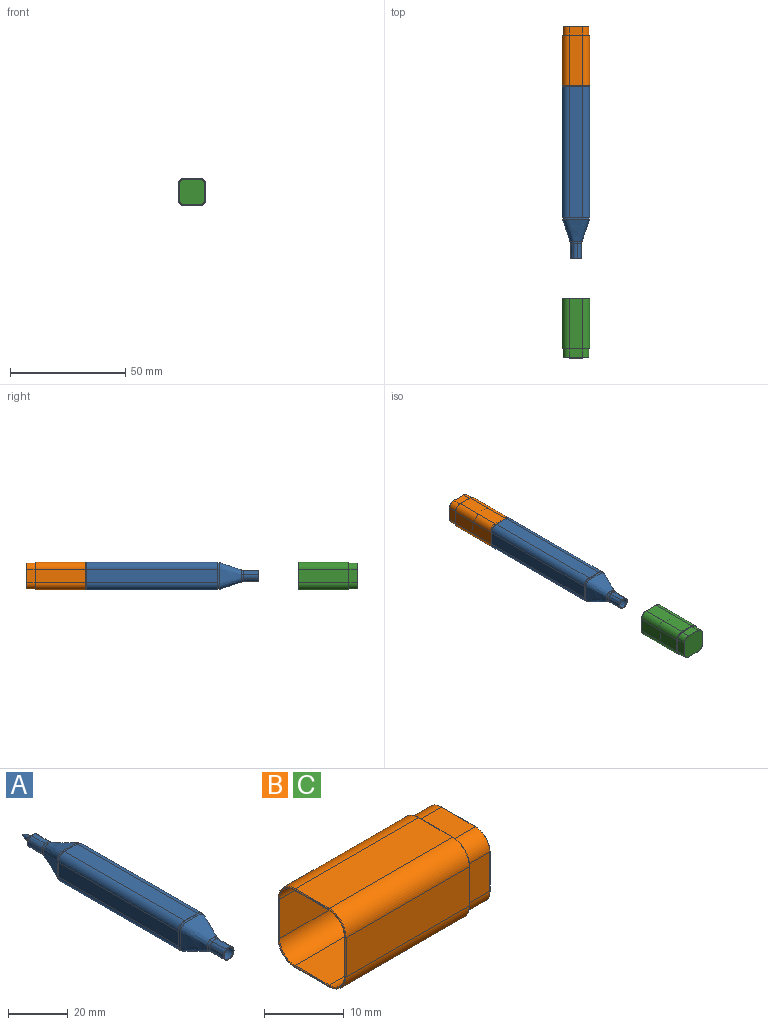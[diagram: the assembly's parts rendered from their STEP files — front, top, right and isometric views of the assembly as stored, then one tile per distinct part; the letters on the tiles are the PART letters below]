
ASSEMBLY  parts=3 mates=1
PART A: 104 faces, bbox 12x98.1x12 mm
  f0: plane 57x6mm, normal (0,0,-1), area 342mm2, adj f1,f3,f7,f9
  f1: plane 12x12mm, normal (0,1,0), area 8mm2, adj f0,f2,f4,f5,f6,f7,f8,f9
  f2: plane 57x6mm, normal (0,0,1), area 342mm2, adj f1,f3,f6,f8
  f3: plane 12x12mm, normal (0,-1,0), area 8mm2, adj f0,f2,f4,f5,f6,f7,f8,f9
  f4: plane 57x6mm, normal (1,0,0), area 342mm2, adj f1,f3,f8,f9
  f5: plane 57x6mm, normal (-1,0,0), area 342mm2, adj f1,f3,f6,f7
  f6: cylinder r=3mm len=57mm, axis (0,-1,0), area 268.6mm2, adj f1,f2,f3,f5
  f7: cylinder r=3mm len=57mm, axis (0,1,0), area 268.6mm2, adj f0,f1,f3,f5
  f8: cylinder r=3mm len=57mm, axis (0,1,0), area 268.6mm2, adj f1,f2,f3,f4
  f9: cylinder r=3mm len=57mm, axis (0,-1,0), area 268.6mm2, adj f0,f1,f3,f4
  f10: plane 6x0.06mm, normal (0,0,-1), area 0.4mm2, adj f1,f11,f17,f18
  f11: cylinder r=2.81mm len=2.81mm, axis (0,-1,0), area 0.3mm2, adj f1,f10,f12,f18
  f12: plane 6x0.06mm, normal (-1,0,0), area 0.4mm2, adj f1,f11,f13,f18
  f13: cylinder r=2.81mm len=2.81mm, axis (0,-1,0), area 0.3mm2, adj f1,f12,f14,f18
  f14: plane 6x0.06mm, normal (0,0,1), area 0.4mm2, adj f1,f13,f15,f18
  f15: cylinder r=2.81mm len=2.81mm, axis (0,-1,0), area 0.3mm2, adj f1,f14,f16,f18
  f16: plane 6x0.06mm, normal (1,0,0), area 0.4mm2, adj f1,f15,f17,f18
  f17: cylinder r=2.81mm len=2.81mm, axis (0,-1,0), area 0.3mm2, adj f1,f10,f16,f18
  f18: plane 11.62x11.62mm, normal (0,1,0), area 4.1mm2, adj f10,f11,f12,f13,f14,f15,f16,f17
  f19: plane 6x0.8mm, normal (1,0,0), area 4.8mm2, adj f18,f20,f26,f45
  f20: cylinder r=2.71mm len=2.71mm, axis (0,-1,0), area 3.4mm2, adj f18,f19,f21,f45
  f21: plane 6x0.8mm, normal (0,0,-1), area 4.8mm2, adj f18,f20,f22,f45
  f22: cylinder r=2.71mm len=2.71mm, axis (0,-1,0), area 3.4mm2, adj f18,f21,f23,f45
  f23: plane 6x0.8mm, normal (-1,0,0), area 4.8mm2, adj f18,f22,f24,f45
  f24: cylinder r=2.71mm len=2.71mm, axis (0,-1,0), area 3.4mm2, adj f18,f23,f25,f45
  f25: plane 6x0.8mm, normal (0,0,1), area 4.8mm2, adj f18,f24,f26,f45
  f26: cylinder r=2.71mm len=2.71mm, axis (0,-1,0), area 3.4mm2, adj f18,f19,f25,f45
  f27: plane 6x0.86mm, normal (1,0,0), area 5.2mm2, adj f3,f28,f34,f35
  f28: cylinder r=2.81mm len=2.81mm, axis (0,1,0), area 3.8mm2, adj f3,f27,f29,f35
  f29: plane 6x0.86mm, normal (0,0,1), area 5.2mm2, adj f3,f28,f30,f35
  f30: cylinder r=2.81mm len=2.81mm, axis (0,1,0), area 3.8mm2, adj f3,f29,f31,f35
  f31: plane 6x0.86mm, normal (-1,0,0), area 5.2mm2, adj f3,f30,f32,f35
  f32: cylinder r=2.81mm len=2.81mm, axis (0,1,0), area 3.8mm2, adj f3,f31,f33,f35
  f33: plane 6x0.86mm, normal (0,0,-1), area 5.2mm2, adj f3,f32,f34,f35
  f34: cylinder r=2.81mm len=2.81mm, axis (0,1,0), area 3.8mm2, adj f3,f27,f33,f35
  f35: bspline ~11.62x11.62mm, area 296.6mm2, adj f27,f28,f29,f30,f31,f32,f33,f34
  f36: extruded ~6.53x1.46mm, area 12.8mm2, adj f37,f43,f44,f91
  f37: extruded ~6.53x1.91mm, area 12.8mm2, adj f36,f38,f44,f93
  f38: extruded ~6.53x1.46mm, area 12.8mm2, adj f37,f39,f44,f92
  f39: extruded ~6.53x1.91mm, area 12.8mm2, adj f38,f40,f44,f90
  f40: extruded ~6.53x1.46mm, area 12.8mm2, adj f39,f41,f44,f88
  f41: extruded ~6.53x1.91mm, area 12.8mm2, adj f40,f42,f44,f86
  f42: extruded ~6.53x1.46mm, area 12.8mm2, adj f41,f43,f44,f87
  f43: extruded ~6.53x1.91mm, area 12.8mm2, adj f36,f42,f44,f89
  f44: plane 5.04x5.04mm, normal (0,-1,0), area 4.4mm2, adj f36,f37,f38,f39,f40,f41,f42,f43
  f45: bspline ~11.42x11.42mm, area 292.4mm2, adj f19,f20,f21,f22,f23,f24,f25,f26
  f46: extruded ~6.52x1.47mm, area 12.8mm2, adj f47,f53,f72,f96
  f47: extruded ~6.52x1.91mm, area 12.8mm2, adj f46,f48,f73,f94
  f48: extruded ~6.52x1.47mm, area 12.8mm2, adj f47,f49,f75,f95
  f49: extruded ~6.52x1.91mm, area 12.8mm2, adj f48,f50,f77,f97
  f50: extruded ~6.52x1.47mm, area 12.8mm2, adj f49,f51,f79,f99
  f51: extruded ~6.52x1.91mm, area 12.8mm2, adj f50,f52,f78,f101
  f52: extruded ~6.52x1.47mm, area 12.8mm2, adj f51,f53,f76,f100
  f53: extruded ~6.52x1.91mm, area 12.8mm2, adj f46,f52,f74,f98
  f54: bspline ~4.94x4.94mm, area 20mm2, adj f64,f65,f66,f67,f68,f69,f70,f71
  f55: extruded ~0.76x0.64mm, area 0.1mm2, adj f56,f62,f63,f70
  f56: extruded ~0.99x0.15mm, area 0.1mm2, adj f55,f57,f63,f68
  f57: extruded ~0.76x0.64mm, area 0.1mm2, adj f56,f58,f63,f66
  f58: extruded ~0.99x0.15mm, area 0.1mm2, adj f57,f59,f63,f64
  f59: extruded ~0.76x0.64mm, area 0.1mm2, adj f58,f60,f63,f65
  f60: extruded ~0.99x0.15mm, area 0.1mm2, adj f59,f61,f63,f67
  f61: extruded ~0.76x0.64mm, area 0.1mm2, adj f60,f62,f63,f69
  f62: extruded ~0.99x0.15mm, area 0.1mm2, adj f55,f61,f63,f71
  f63: plane 2.6x2.6mm, normal (0,1,0), area 1.9mm2, adj f55,f56,f57,f58,f59,f60,f61,f62
  f64: bspline ~1.13x0.17mm, area 0mm2, adj f54,f58,f65,f66
  f65: bspline ~0.85x0.75mm, area 0mm2, adj f54,f59,f64,f67
  f66: bspline ~0.85x0.75mm, area 0mm2, adj f54,f57,f64,f68
  f67: bspline ~1.13x0.17mm, area 0mm2, adj f54,f60,f65,f69
  f68: bspline ~1.13x0.17mm, area 0mm2, adj f54,f56,f66,f70
  f69: bspline ~0.85x0.75mm, area 0mm2, adj f54,f61,f67,f71
  f70: bspline ~0.85x0.75mm, area 0mm2, adj f54,f55,f68,f71
  f71: bspline ~1.13x0.17mm, area 0mm2, adj f54,f62,f69,f70
  f72: bspline ~1.91x1.6mm, area 0.1mm2, adj f46,f54,f73,f74
  f73: bspline ~2.47x0.46mm, area 0.1mm2, adj f47,f54,f72,f75
  f74: bspline ~2.47x0.46mm, area 0.1mm2, adj f53,f54,f72,f76
  f75: bspline ~1.91x1.6mm, area 0.1mm2, adj f48,f54,f73,f77
  f76: bspline ~1.91x1.6mm, area 0.1mm2, adj f52,f54,f74,f78
  f77: bspline ~2.47x0.46mm, area 0.1mm2, adj f49,f54,f75,f79
  f78: bspline ~2.47x0.46mm, area 0.1mm2, adj f51,f54,f76,f79
  f79: bspline ~1.91x1.6mm, area 0.1mm2, adj f50,f54,f77,f78
  f80: cylinder r=1.04mm len=25mm, axis (0,1,0), area 164.1mm2, adj f63,f81
  f81: plane 2.09x2.09mm, normal (0,1,0), area 0.3mm2, adj f80,f82
  f82: cylinder r=1mm len=25.5mm, axis (0,-1,0), area 160.2mm2, adj f81,f84
  f83: plane 0.03x0.03mm, normal (0,1,0), area 0mm2, adj f85
  f84: bspline ~3.37x2mm, area 14.2mm2, adj f82,f85
  f85: bspline ~0.13x0.13mm, area 0mm2, adj f83,f84
  f86: bspline ~2.32x1.15mm, area 2.1mm2, adj f35,f41,f87,f88
  f87: bspline ~1.66x1.49mm, area 2.4mm2, adj f35,f42,f86,f89
  f88: bspline ~1.66x1.49mm, area 2.4mm2, adj f35,f40,f86,f90
  f89: bspline ~2.32x1.15mm, area 2.1mm2, adj f35,f43,f87,f91
  f90: bspline ~2.32x1.15mm, area 2.1mm2, adj f35,f39,f88,f92
  f91: bspline ~1.66x1.49mm, area 2.4mm2, adj f35,f36,f89,f93
  f92: bspline ~1.66x1.49mm, area 2.4mm2, adj f35,f38,f90,f93
  f93: bspline ~2.38x1.16mm, area 2.1mm2, adj f35,f37,f91,f92
  f94: bspline ~2.31x1.13mm, area 2.1mm2, adj f45,f47,f95,f96
  f95: bspline ~1.66x1.47mm, area 2.4mm2, adj f45,f48,f94,f97
  f96: bspline ~1.66x1.47mm, area 2.4mm2, adj f45,f46,f94,f98
  f97: bspline ~2.31x1.13mm, area 2.1mm2, adj f45,f49,f95,f99
  f98: bspline ~2.31x1.13mm, area 2.1mm2, adj f45,f53,f96,f100
  f99: bspline ~1.66x1.47mm, area 2.4mm2, adj f45,f50,f97,f101
  f100: bspline ~1.66x1.47mm, area 2.4mm2, adj f45,f52,f98,f101
  f101: bspline ~2.31x1.13mm, area 2.1mm2, adj f45,f51,f99,f100
  f102: cylinder r=2.2mm len=25mm, axis (0,-1,0), area 346.2mm2, adj f44,f103
  f103: plane 4.41x4.41mm, normal (0,-1,0), area 15.3mm2, adj f102
PART B: 73 faces, bbox 26x14x14 mm
  f0: plane 21.8x6mm, normal (0,1,0), area 130.8mm2, adj f1,f7,f43,f51
  f1: cylinder r=3mm len=21.8mm, axis (-1,0,0), area 102.7mm2, adj f0,f2,f41,f49
  f2: plane 21.8x6mm, normal (0,0,1), area 130.8mm2, adj f1,f3,f40,f48
  f3: cylinder r=3mm len=21.8mm, axis (-1,0,0), area 102.7mm2, adj f2,f4,f42,f50
  f4: plane 21.8x6mm, normal (0,-1,0), area 130.8mm2, adj f3,f5,f44,f52
  f5: cylinder r=3mm len=21.8mm, axis (-1,0,0), area 102.7mm2, adj f4,f6,f46,f54
  f6: plane 21.8x6mm, normal (0,0,-1), area 130.8mm2, adj f5,f7,f47,f55
  f7: cylinder r=3mm len=21.8mm, axis (-1,0,0), area 102.7mm2, adj f0,f6,f45,f53
  f8: plane 11.8x11.8mm, normal (1,0,0), area 10.8mm2, adj f48,f49,f50,f51,f52,f53,f54,f55
  f9: plane 11.8x11.8mm, normal (-1,0,0), area 2.1mm2, adj f32,f33,f34,f35,f36,f37,f38,f39
  f10: plane 6x3.9mm, normal (0,0,-1), area 23.4mm2, adj f11,f17,f59,f68
  f11: cylinder r=2.6mm len=3.9mm, axis (-1,0,0), area 15.9mm2, adj f10,f12,f61,f66
  f12: plane 6x3.9mm, normal (0,1,0), area 23.4mm2, adj f11,f13,f63,f64
  f13: cylinder r=2.6mm len=3.9mm, axis (-1,0,0), area 15.9mm2, adj f12,f14,f62,f65
  f14: plane 6x3.9mm, normal (0,0,1), area 23.4mm2, adj f13,f15,f60,f67
  f15: cylinder r=2.6mm len=3.9mm, axis (-1,0,0), area 15.9mm2, adj f14,f16,f58,f69
  f16: plane 6x3.9mm, normal (0,-1,0), area 23.4mm2, adj f15,f17,f56,f71
  f17: cylinder r=2.6mm len=3.9mm, axis (-1,0,0), area 15.9mm2, adj f10,f16,f57,f70
  f18: plane 11.08x11.08mm, normal (1,0,0), area 117.2mm2, adj f64,f65,f66,f67,f68,f69,f70,f71
  f19: plane 11.65x6mm, normal (0,0,-1), area 68.4mm2, adj f20,f26,f31,f36
  f20: cylinder r=2.75mm len=10.91mm, axis (-1,0,0), area 45.7mm2, adj f19,f21,f31,f34
  f21: plane 11.66x6mm, normal (0,-1,0), area 68.4mm2, adj f20,f22,f31,f32
  f22: cylinder r=2.75mm len=10.91mm, axis (-1,0,0), area 45.7mm2, adj f21,f23,f31,f33
  f23: plane 11.66x6mm, normal (0,0,1), area 68.4mm2, adj f22,f24,f31,f35
  f24: cylinder r=2.75mm len=10.91mm, axis (-1,0,0), area 45.7mm2, adj f23,f25,f31,f37
  f25: plane 11.66x6mm, normal (0,1,0), area 68.4mm2, adj f24,f26,f31,f39
  f26: cylinder r=2.75mm len=10.91mm, axis (-1,0,0), area 45.7mm2, adj f19,f25,f31,f38
  f27: cylinder r=3.4mm len=6.8mm, axis (-1,0,0), area 106.8mm2, adj f28,f30
  f28: plane 7x7mm, normal (-1,0,0), area 2.2mm2, adj f27,f29
  f29: cylinder r=3.5mm len=7mm, axis (-1,0,0), area 61.4mm2, adj f28,f72
  f30: cone r=0mm half-angle=59deg, axis (-1,0,0), area 42.4mm2, adj f27
  f31: cone r=3.5mm half-angle=45deg, axis (-1,0,0), area 118.8mm2, adj f19,f20,f21,f22,f23,f24,f25,f26
  f32: cylinder r=0.1mm len=6mm, axis (0,0,-1), area 0.9mm2, adj f9,f21,f33,f34
  f33: torus R=2.85mm, axis (1,0,0), area 0.7mm2, adj f9,f22,f32,f35
  f34: torus R=2.85mm, axis (1,0,0), area 0.7mm2, adj f9,f20,f32,f36
  f35: cylinder r=0.1mm len=6mm, axis (0,-1,0), area 0.9mm2, adj f9,f23,f33,f37
  f36: cylinder r=0.1mm len=6mm, axis (0,1,0), area 0.9mm2, adj f9,f19,f34,f38
  f37: torus R=2.85mm, axis (1,0,0), area 0.7mm2, adj f9,f24,f35,f39
  f38: torus R=2.85mm, axis (1,0,0), area 0.7mm2, adj f9,f26,f36,f39
  f39: cylinder r=0.1mm len=6mm, axis (0,0,1), area 0.9mm2, adj f9,f25,f37,f38
  f40: cylinder r=0.1mm len=6mm, axis (0,-1,0), area 0.9mm2, adj f2,f9,f41,f42
  f41: torus R=2.9mm, axis (1,0,0), area 0.7mm2, adj f1,f9,f40,f43
  f42: torus R=2.9mm, axis (1,0,0), area 0.7mm2, adj f3,f9,f40,f44
  f43: cylinder r=0.1mm len=6mm, axis (0,0,1), area 0.9mm2, adj f0,f9,f41,f45
  f44: cylinder r=0.1mm len=6mm, axis (0,0,-1), area 0.9mm2, adj f4,f9,f42,f46
  f45: torus R=2.9mm, axis (1,0,0), area 0.7mm2, adj f7,f9,f43,f47
  f46: torus R=2.9mm, axis (1,0,0), area 0.7mm2, adj f5,f9,f44,f47
  f47: cylinder r=0.1mm len=6mm, axis (0,1,0), area 0.9mm2, adj f6,f9,f45,f46
  f48: cylinder r=0.1mm len=6mm, axis (0,1,0), area 0.9mm2, adj f2,f8,f49,f50
  f49: torus R=2.9mm, axis (1,0,0), area 0.7mm2, adj f1,f8,f48,f51
  f50: torus R=2.9mm, axis (1,0,0), area 0.7mm2, adj f3,f8,f48,f52
  f51: cylinder r=0.1mm len=6mm, axis (0,0,-1), area 0.9mm2, adj f0,f8,f49,f53
  f52: cylinder r=0.1mm len=6mm, axis (0,0,1), area 0.9mm2, adj f4,f8,f50,f54
  f53: torus R=2.9mm, axis (1,0,0), area 0.7mm2, adj f7,f8,f51,f55
  f54: torus R=2.9mm, axis (1,0,0), area 0.7mm2, adj f5,f8,f52,f55
  f55: cylinder r=0.1mm len=6mm, axis (0,-1,0), area 0.9mm2, adj f6,f8,f53,f54
  f56: plane 6x0.04mm, normal (0.71,-0.71,0), area 0.3mm2, adj f8,f16,f57,f58
  f57: cone r=2.6mm half-angle=45deg, axis (-1,0,0), area 0.2mm2, adj f8,f17,f56,f59
  f58: cone r=2.6mm half-angle=45deg, axis (-1,0,0), area 0.2mm2, adj f8,f15,f56,f60
  f59: plane 6x0.04mm, normal (0.71,0,-0.71), area 0.3mm2, adj f8,f10,f57,f61
  f60: plane 6x0.04mm, normal (0.71,0,0.71), area 0.3mm2, adj f8,f14,f58,f62
  f61: cone r=2.6mm half-angle=45deg, axis (-1,0,0), area 0.2mm2, adj f8,f11,f59,f63
  f62: cone r=2.6mm half-angle=45deg, axis (-1,0,0), area 0.2mm2, adj f8,f13,f60,f63
  f63: plane 6x0.04mm, normal (0.71,0.71,0), area 0.3mm2, adj f8,f12,f61,f62
  f64: cylinder r=0.06mm len=6mm, axis (0,0,-1), area 0.6mm2, adj f12,f18,f65,f66
  f65: torus R=2.54mm, axis (1,0,0), area 0.4mm2, adj f13,f18,f64,f67
  f66: torus R=2.54mm, axis (1,0,0), area 0.4mm2, adj f11,f18,f64,f68
  f67: cylinder r=0.06mm len=6mm, axis (0,1,0), area 0.6mm2, adj f14,f18,f65,f69
  f68: cylinder r=0.06mm len=6mm, axis (0,-1,0), area 0.6mm2, adj f10,f18,f66,f70
  f69: torus R=2.54mm, axis (1,0,0), area 0.4mm2, adj f15,f18,f67,f71
  f70: torus R=2.54mm, axis (1,0,0), area 0.4mm2, adj f17,f18,f68,f71
  f71: cylinder r=0.06mm len=6mm, axis (0,0,1), area 0.6mm2, adj f16,f18,f69,f70
  f72: torus R=4mm, axis (1,0,0), area 8.8mm2, adj f29,f31
PART C: same geometry as B
PLACE A at identity
PLACE B rot(axis=(0.58,0.58,0.58),120deg) t=(0,39.56,0)mm
PLACE C rot(axis=(-0.58,0.58,-0.58),120deg) t=(0,-74.5,0)mm
MATE fastened B.f27 <-> A.f82  axis (0,-1,0) through (0,28.56,0)mm
